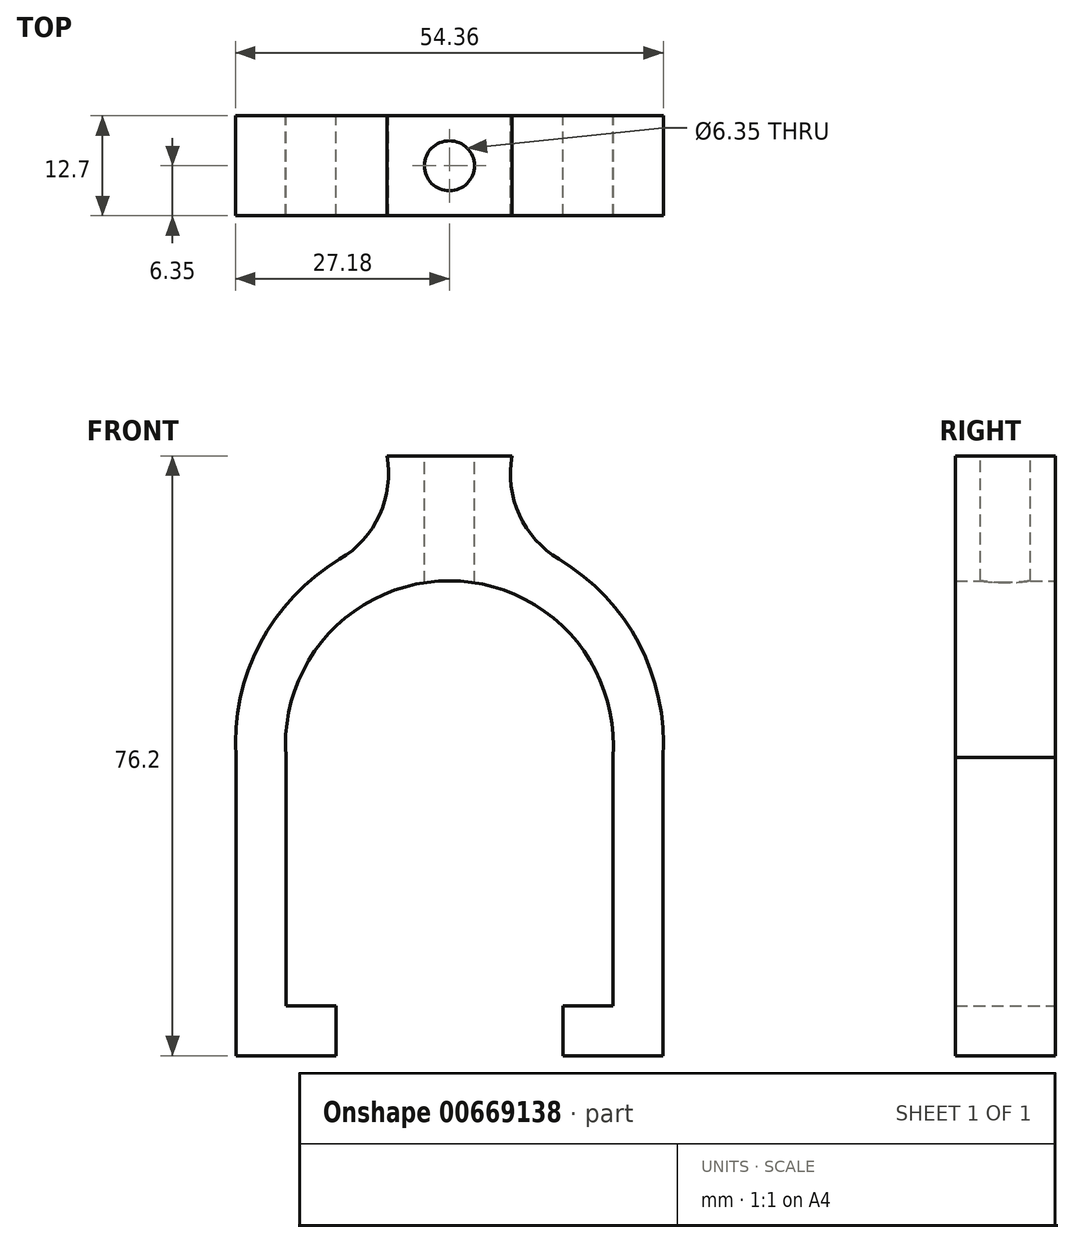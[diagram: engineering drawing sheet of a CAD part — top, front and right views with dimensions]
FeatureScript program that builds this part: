
annotation { "Feature Type Name" : "Feature", "Feature Type Description" : "" }
export const myFeature = defineFeature(function(context is Context, id is Id, definition is map)
    precondition{}
    {
        {
            var Q0;
            Q0=qCreatedBy(makeId("Front.planeOp"),FACE);
            var sketch = newSketch(context, id + "F0", { "sketchPlane" : qUnion([Q0])});
            skLineSegment(sketch, "E0", {"start": v(-20.76, -1.63) * mm, "end": v(-20.76, -33.15) * mm});
            skLineSegment(sketch, "E1", {"start": v(20.76, -1.63) * mm, "end": v(20.76, -33.15) * mm});
            skArc(sketch, "E2", {"start": v(20.76, -1.63) * mm, "mid": v(0, 20.83) * mm, "end": v(-20.76, -1.63) * mm});
            skLineSegment(sketch, "E3", {"start": v(-20.76, -33.15) * mm, "end": v(-14.41, -33.15) * mm});
            skLineSegment(sketch, "E4", {"start": v(-14.41, -33.15) * mm, "end": v(-14.41, -39.5) * mm});
            skLineSegment(sketch, "E5", {"start": v(-14.41, -39.5) * mm, "end": v(-27.11, -39.5) * mm});
            skLineSegment(sketch, "E6", {"start": v(-27.11, -39.5) * mm, "end": v(-27.11, -1.63) * mm});
            skLineSegment(sketch, "E7", {"start": v(20.76, -33.15) * mm, "end": v(14.41, -33.15) * mm});
            skLineSegment(sketch, "E8", {"start": v(14.41, -33.15) * mm, "end": v(14.41, -39.5) * mm});
            skLineSegment(sketch, "E9", {"start": v(14.41, -39.5) * mm, "end": v(27.11, -39.5) * mm});
            skLineSegment(sketch, "E10", {"start": v(27.11, -39.5) * mm, "end": v(27.11, -1.63) * mm});
            skLineSegment(sketch, "E11", {"start": v(-7.94, 36.7) * mm, "end": v(0, 36.7) * mm});
            skLineSegment(sketch, "E12", {"start": v(0, 36.7) * mm, "end": v(7.94, 36.7) * mm});
            skArc(sketch, "E13", {"start": v(-27.11, -1.63) * mm, "mid": v(-24.08, 12.83) * mm, "end": v(-13.93, 23.57) * mm});
            skArc(sketch, "E14", {"start": v(-7.94, 36.7) * mm, "mid": v(-8.89, 29.2) * mm, "end": v(-13.93, 23.57) * mm});
            skArc(sketch, "E15", {"start": v(27.11, -1.63) * mm, "mid": v(24.08, 12.83) * mm, "end": v(13.93, 23.57) * mm});
            skArc(sketch, "E16", {"start": v(7.94, 36.7) * mm, "mid": v(8.89, 29.2) * mm, "end": v(13.93, 23.57) * mm});
            skSolve(sketch);
        }
        {
            var Q0;
            Q0 = qSketchRegion(id + "F0", true);
            extrude(context, id + "F1", {"entities" : qUnion([Q0]), "depth" : 12.7 * mm, "offsetDistance" : 25.4 * mm});
        }
        {
            var Q0;
            Q0=makeQuery(id+"F1.opExtrude","SWEPT_FACE",FACE,{"disambiguationData":[OSD([sQuery(id+"F0.wireOp",EDGE,"E11"),sQuery(id+"F0.wireOp",EDGE,"E12")])]});
            var sketch = newSketch(context, id + "F2", { "sketchPlane" : qUnion([Q0])});
            skCircle(sketch, "E17", {"center": v(0, -6.35) * mm, "radius": 3.18 * mm});
            skSolve(sketch);
        }
        {
            var Q0;
            Q0 = qSketchRegion(id + "F2", true);
            extrude(context, id + "F3", {"entities" : qUnion([Q0]), "operationType" : NewBodyOperationType.REMOVE, "oppositeDirection" : true, "depth" : 25.4 * mm, "offsetDistance" : 25.4 * mm});
        }
    });
